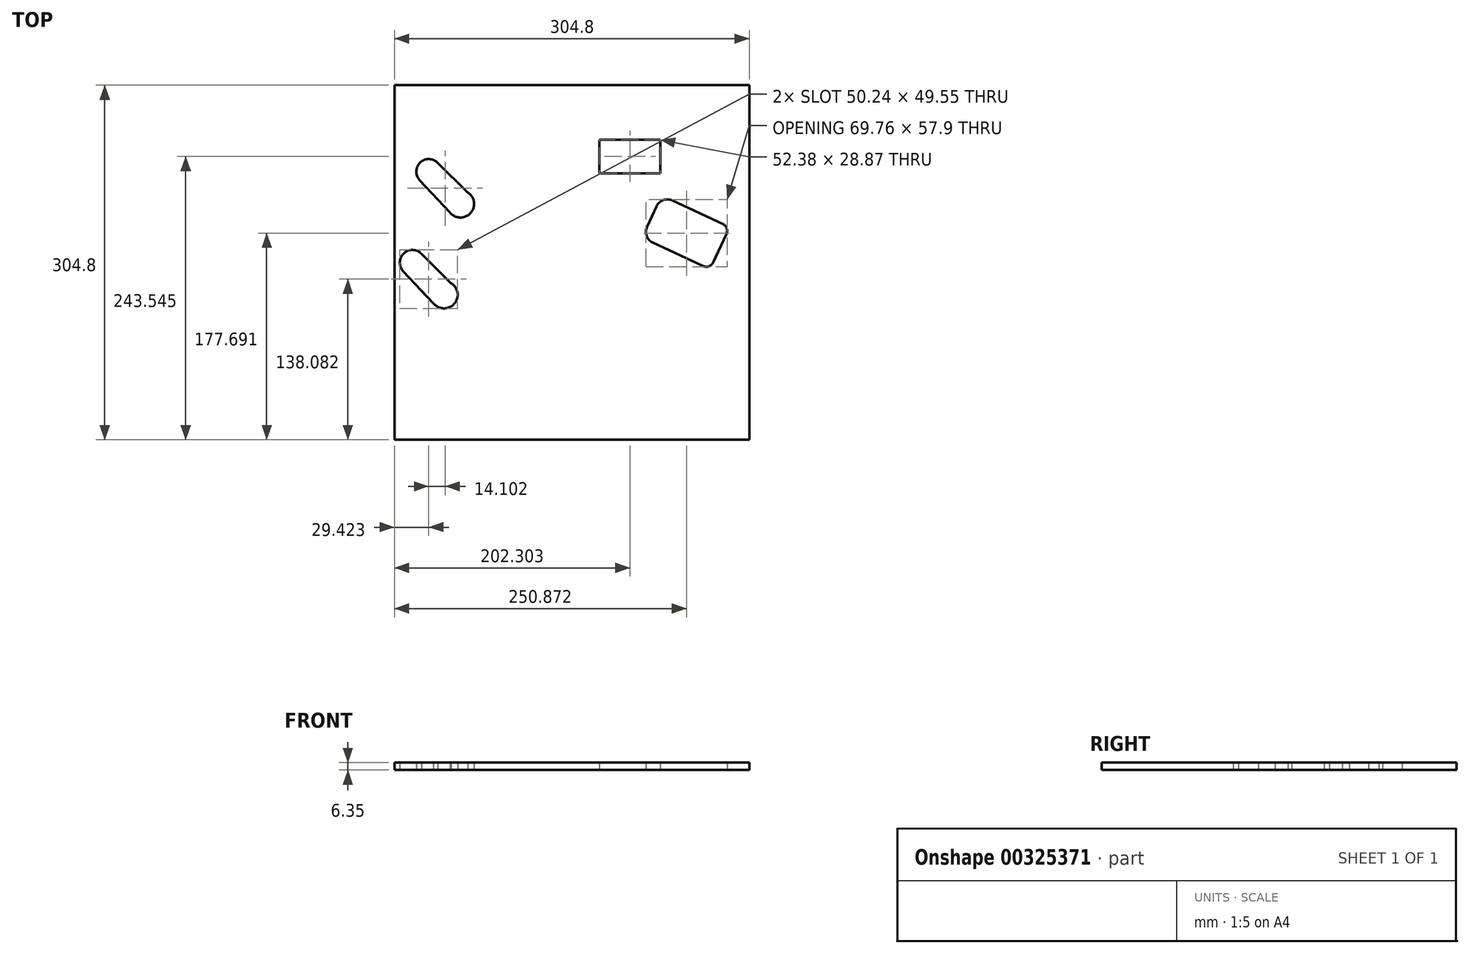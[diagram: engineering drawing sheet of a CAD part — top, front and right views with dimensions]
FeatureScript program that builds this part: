
annotation { "Feature Type Name" : "Feature", "Feature Type Description" : "" }
export const myFeature = defineFeature(function(context is Context, id is Id, definition is map)
    precondition{}
    {
        {
            var Q0;
            Q0=qCreatedBy(makeId("Top.planeOp"),FACE);
            var sketch = newSketch(context, id + "F0", { "sketchPlane" : qUnion([Q0])});
            skLineSegment(sketch, "E0.bottom", {"start": v(152.4, -152.4) * mm, "end": v(-152.4, -152.4) * mm});
            skLineSegment(sketch, "E0.top", {"start": v(152.4, 152.4) * mm, "end": v(-152.4, 152.4) * mm});
            skLineSegment(sketch, "E0.left", {"start": v(152.4, -152.4) * mm, "end": v(152.4, 152.4) * mm});
            skLineSegment(sketch, "E0.right", {"start": v(-152.4, -152.4) * mm, "end": v(-152.4, 152.4) * mm});
            skPoint(sketch, "E0.middle", {"position": v(0, 0) * mm});
            skCircle(sketch, "E1", {"center": v(-136.95, 0) * mm, "radius": 10.8 * mm});
            skCircle(sketch, "E2", {"center": v(-109.78, -27.75) * mm, "radius": 11.7 * mm});
            skLineSegment(sketch, "E3", {"start": v(-117.67, -36.38) * mm, "end": v(-144.84, -7.39) * mm});
            skLineSegment(sketch, "E4", {"start": v(-129.61, 7.93) * mm, "end": v(-103.56, -17.84) * mm});
            skCircle(sketch, "E5", {"center": v(-122.85, 78.1) * mm, "radius": 10.8 * mm});
            skCircle(sketch, "E6", {"center": v(-95.68, 50.36) * mm, "radius": 11.7 * mm});
            skLineSegment(sketch, "E7", {"start": v(-103.56, 41.73) * mm, "end": v(-130.73, 70.72) * mm});
            skLineSegment(sketch, "E8", {"start": v(-115.51, 86.04) * mm, "end": v(-89.46, 60.27) * mm});
            skLineSegment(sketch, "E9.bottom", {"start": v(23.71, 105.58) * mm, "end": v(76.1, 105.58) * mm});
            skLineSegment(sketch, "E9.top", {"start": v(23.71, 76.71) * mm, "end": v(76.1, 76.71) * mm});
            skLineSegment(sketch, "E9.left", {"start": v(23.71, 105.58) * mm, "end": v(23.71, 76.71) * mm});
            skLineSegment(sketch, "E9.right", {"start": v(76.1, 105.58) * mm, "end": v(76.1, 76.71) * mm});
            skLineSegment(sketch, "E10.bottom", {"start": v(86.3, 53.3) * mm, "end": v(129.7, 33.06) * mm});
            skLineSegment(sketch, "E10.top", {"start": v(69.45, 17.17) * mm, "end": v(112.85, -3.07) * mm});
            skLineSegment(sketch, "E10.left", {"start": v(72.8, 48.38) * mm, "end": v(64.53, 30.67) * mm});
            skLineSegment(sketch, "E10.right", {"start": v(132.76, 24.62) * mm, "end": v(121.28, 0) * mm});
            skPoint(sketch, "E11.visualSharp", {"position": v(77.09, 57.6) * mm});
            skArc(sketch, "E11.filletArc", {"start": v(86.3, 53.3) * mm, "mid": v(78.53, 53.64) * mm, "end": v(72.8, 48.38) * mm});
            skPoint(sketch, "E12.visualSharp", {"position": v(60.24, 21.46) * mm});
            skArc(sketch, "E12.filletArc", {"start": v(64.53, 30.67) * mm, "mid": v(64.2, 22.9) * mm, "end": v(69.45, 17.17) * mm});
            skPoint(sketch, "E13.visualSharp", {"position": v(118.6, -5.75) * mm});
            skArc(sketch, "E13.filletArc", {"start": v(112.85, -3.07) * mm, "mid": v(117.7, -3.28) * mm, "end": v(121.28, 0) * mm});
            skPoint(sketch, "E14.visualSharp", {"position": v(135.45, 30.38) * mm});
            skArc(sketch, "E14.filletArc", {"start": v(132.76, 24.62) * mm, "mid": v(132.98, 29.48) * mm, "end": v(129.7, 33.06) * mm});
            skSolve(sketch);
        }
        {
            var Q0;
            Q0 = qSketchRegion(id + "F0", true);
            extrude(context, id + "F1", {"entities" : qUnion([Q0]), "depth" : 6.35 * mm});
        }
    });
